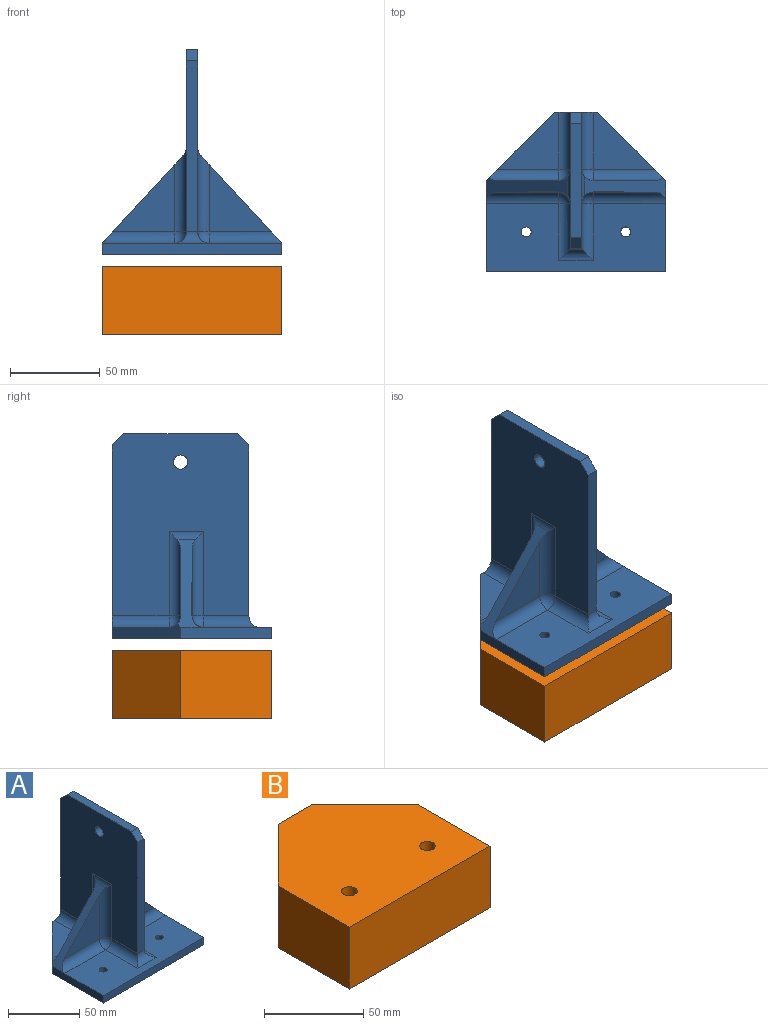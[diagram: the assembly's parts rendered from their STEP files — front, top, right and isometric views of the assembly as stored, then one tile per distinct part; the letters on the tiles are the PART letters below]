
ASSEMBLY  parts=2 mates=1
PART A: 54 faces, bbox 100x88.9x114.3 mm
  f0: plane 100x88.9mm, normal (0,0,-1), area 7316.2mm2, adj f6,f7,f8,f10,f19,f20,f21,f22
  f1: plane 101.6x76.2mm, normal (-1,0,0), area 6758.9mm2, adj f9,f10,f11,f16,f23,f24,f35,f38
  f2: plane 101.6x76.2mm, normal (1,0,0), area 6758.9mm2, adj f9,f10,f11,f16,f23,f24,f25,f28
  f3: plane 100x38.1mm, normal (0,0,1), area 3156.1mm2, adj f6,f7,f8,f21,f22,f31,f33,f34
  f4: plane 37.56x34.62mm, normal (0,1,0), area 650.2mm2, adj f12,f26,f28
  f5: plane 37.56x34.62mm, normal (0,1,0), area 650.2mm2, adj f14,f40,f41
  f6: plane 50.8x6.35mm, normal (-1,0,0), area 322.6mm2, adj f0,f3,f7,f14,f19
  f7: plane 100x6.35mm, normal (0,-1,0), area 635mm2, adj f0,f3,f6,f8
  f8: plane 50.8x6.35mm, normal (1,0,0), area 322.6mm2, adj f0,f3,f7,f12,f20
  f9: plane 95.25x6.35mm, normal (0,-1,0), area 604.8mm2, adj f1,f2,f23,f34
  f10: plane 107.95x23.8mm, normal (0,1,0), area 813.6mm2, adj f0,f1,f2,f17,f18,f19,f20,f24
  f11: plane 63.5x6.35mm, normal (0,0,1), area 403.2mm2, adj f1,f2,f23,f24
  f12: plane 48.98x45.14mm, normal (0.74,0,0.68), area 449.1mm2, adj f4,f8,f13,f20,f26,f28,f29,f30
  f13: plane 37.56x34.62mm, normal (0,-1,0), area 650.2mm2, adj f12,f30,f31
  f14: plane 48.98x45.14mm, normal (-0.74,0,0.68), area 449.1mm2, adj f5,f6,f15,f19,f36,f38,f39,f40
  f15: plane 37.56x34.62mm, normal (0,-1,0), area 650.2mm2, adj f14,f36,f38
  f16: cylinder r=3.94mm len=7.87mm, axis (-1,0,0), area 157.1mm2, adj f1,f2
  f17: plane 34.13x31.75mm, normal (0,0,1), area 579.4mm2, adj f10,f20,f25,f26
  f18: plane 34.13x31.75mm, normal (0,0,1), area 579.4mm2, adj f10,f19,f41,f43
  f19: plane 38.1x38.1mm, normal (-0.71,0.71,0), area 348.5mm2, adj f0,f6,f10,f14,f18,f41
  f20: plane 38.1x38.1mm, normal (0.71,0.71,0), area 348.5mm2, adj f0,f8,f10,f12,f17,f26
  f21: cylinder r=2.79mm len=6.35mm, axis (0,0,1), area 111.5mm2, adj f0,f3
  f22: cylinder r=2.79mm len=6.35mm, axis (0,0,1), area 111.5mm2, adj f0,f3
  f23: plane 6.35x6.35mm, normal (0,-0.71,0.71), area 57mm2, adj f1,f2,f9,f11
  f24: plane 6.35x6.35mm, normal (0,0.71,0.71), area 57mm2, adj f1,f2,f10,f11
  f25: cylinder r=6.35mm len=31.75mm, axis (0,1,0), area 316.7mm2, adj f2,f10,f17,f27
  f26: cylinder r=6.35mm len=38.69mm, axis (1,0,0), area 365.5mm2, adj f4,f12,f17,f20,f27
  f27: sphere r=6.35mm, area 63.3mm2, adj f25,f26,f28
  f28: cylinder r=6.35mm len=46.93mm, axis (0,0,1), area 422.4mm2, adj f2,f4,f12,f27,f29
  f29: cylinder r=6.35mm len=19.05mm, axis (0,1,0), area 68.7mm2, adj f2,f12,f28,f30
  f30: cylinder r=6.35mm len=46.93mm, axis (0,0,-1), area 422.4mm2, adj f2,f12,f13,f29,f32
  f31: cylinder r=6.35mm len=40.48mm, axis (1,0,0), area 382.5mm2, adj f3,f12,f13,f32
  f32: sphere r=6.35mm, area 63.3mm2, adj f30,f31,f33
  f33: cylinder r=6.35mm len=31.75mm, axis (0,-1,0), area 276.4mm2, adj f2,f3,f32,f34
  f34: cylinder r=6.35mm len=19.05mm, axis (-1,0,0), area 109.4mm2, adj f3,f9,f33,f35
  f35: cylinder r=6.35mm len=31.75mm, axis (0,1,0), area 276.4mm2, adj f1,f3,f34,f37
  f36: cylinder r=6.35mm len=40.48mm, axis (-1,0,0), area 382.5mm2, adj f3,f14,f15,f37
  f37: sphere r=6.35mm, area 63.3mm2, adj f35,f36,f38
  f38: cylinder r=6.35mm len=46.93mm, axis (0,0,1), area 422.4mm2, adj f1,f14,f15,f37,f39
  f39: cylinder r=6.35mm len=19.05mm, axis (0,1,0), area 68.7mm2, adj f1,f14,f38,f40
  f40: cylinder r=6.35mm len=46.93mm, axis (0,0,-1), area 422.4mm2, adj f1,f5,f14,f39,f42
  f41: cylinder r=6.35mm len=38.69mm, axis (1,0,0), area 365.5mm2, adj f5,f14,f18,f19,f42
  f42: sphere r=6.35mm, area 63.3mm2, adj f40,f41,f43
  f43: cylinder r=6.35mm len=31.75mm, axis (0,-1,0), area 316.7mm2, adj f1,f10,f18,f42
  f44: plane 104.14x16mm, normal (1,0,0), area 1666.4mm2, adj f0,f45,f47,f48
  f45: plane 104.14x2.29mm, normal (0,-1,0), area 238.1mm2, adj f0,f44,f46,f48
  f46: plane 104.14x16mm, normal (-1,0,0), area 1666.4mm2, adj f0,f45,f47,f48
  f47: plane 104.14x2.29mm, normal (0,1,0), area 238.1mm2, adj f0,f44,f46,f48
  f48: plane 16x2.29mm, normal (0,0,-1), area 36.6mm2, adj f44,f45,f46,f47
  f49: plane 104.14x16mm, normal (-1,0,0), area 1666.4mm2, adj f0,f50,f52,f53
  f50: plane 104.14x2.29mm, normal (0,1,0), area 238.1mm2, adj f0,f49,f51,f53
  f51: plane 104.14x16mm, normal (1,0,0), area 1666.4mm2, adj f0,f50,f52,f53
  f52: plane 104.14x2.29mm, normal (0,-1,0), area 238.1mm2, adj f0,f49,f51,f53
  f53: plane 16x2.29mm, normal (0,0,-1), area 36.6mm2, adj f49,f50,f51,f52
PART B: 10 faces, bbox 100x88.9x38.1 mm
  f0: plane 38.1x23.8mm, normal (0,1,0), area 906.8mm2, adj f4,f5,f6,f7
  f1: plane 50.8x38.1mm, normal (-1,0,0), area 1935.5mm2, adj f2,f4,f5,f6
  f2: plane 100x38.1mm, normal (0,-1,0), area 3810mm2, adj f1,f3,f4,f5
  f3: plane 50.8x38.1mm, normal (1,0,0), area 1935.5mm2, adj f2,f4,f5,f7
  f4: plane 100x88.9mm, normal (0,0,1), area 7341mm2, adj f0,f1,f2,f3,f6,f7,f8,f9
  f5: plane 100x88.9mm, normal (0,0,-1), area 7341mm2, adj f0,f1,f2,f3,f6,f7,f8,f9
  f6: plane 38.1x38.1mm, normal (-0.71,0.71,0), area 2052.9mm2, adj f0,f1,f4,f5
  f7: plane 38.1x38.1mm, normal (0.71,0.71,0), area 2052.9mm2, adj f0,f3,f4,f5
  f8: cylinder r=3.94mm len=38.1mm, axis (0,0,-1), area 942.5mm2, adj f4,f5
  f9: cylinder r=3.94mm len=38.1mm, axis (0,0,-1), area 942.5mm2, adj f4,f5
PLACE A t=(0.15,-19.28,-57.15)mm
PLACE B t=(0.15,-0.23,-101.6)mm
MATE parallel B.f4 <-> A.f0  axis (0,0,1) through (-49.85,-44.68,-63.5)mm
